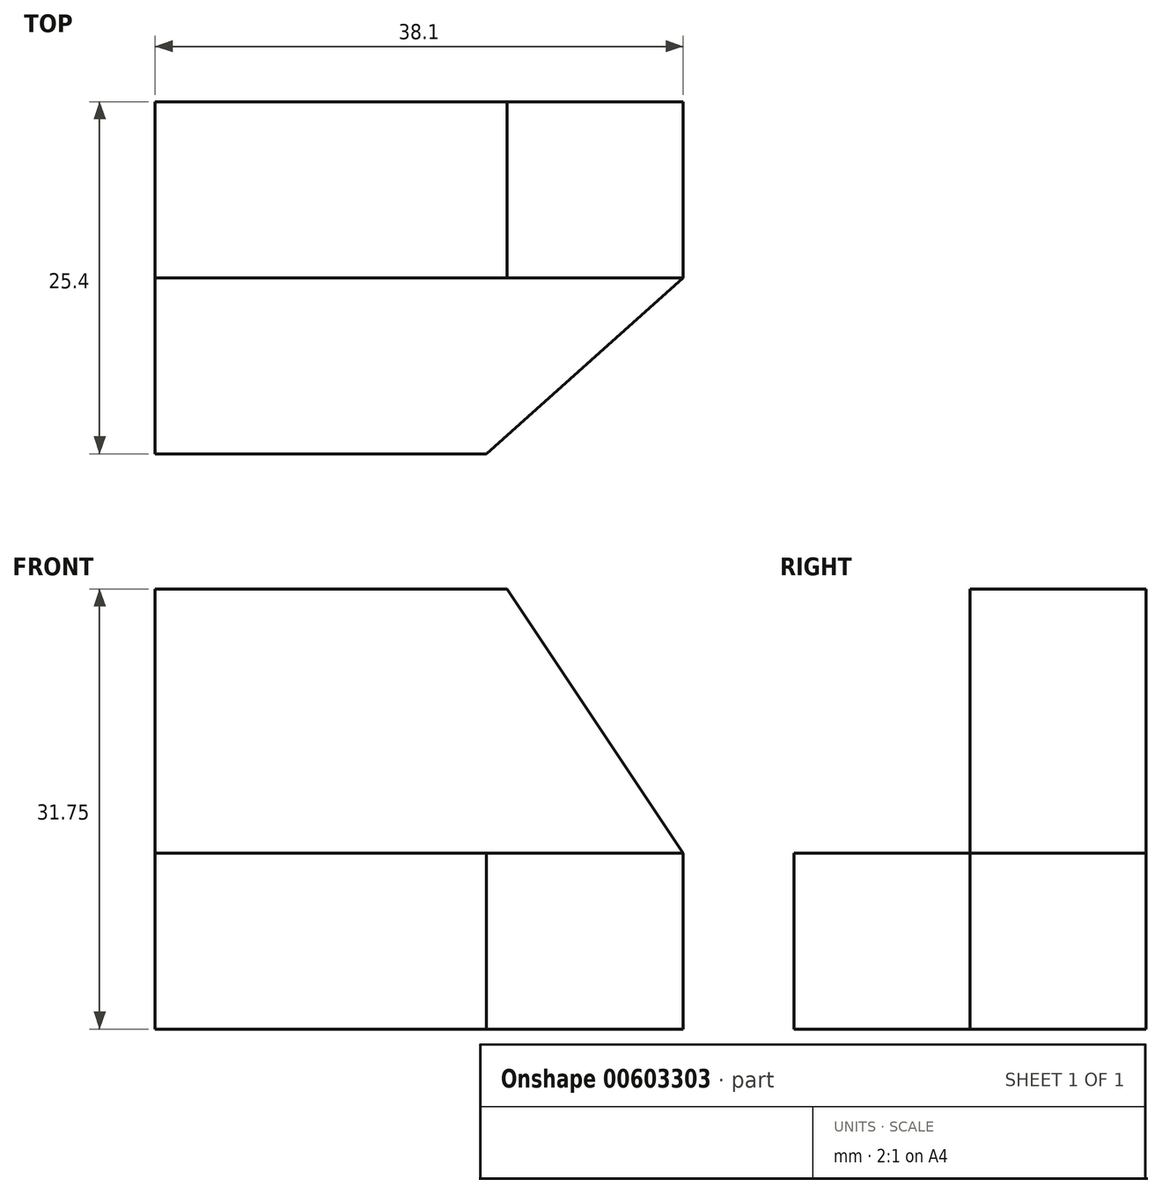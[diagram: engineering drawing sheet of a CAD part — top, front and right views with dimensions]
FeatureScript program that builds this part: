
annotation { "Feature Type Name" : "Feature", "Feature Type Description" : "" }
export const myFeature = defineFeature(function(context is Context, id is Id, definition is map)
    precondition{}
    {
        {
            var Q0;
            Q0=qCreatedBy(makeId("Front.planeOp"),FACE);
            var sketch = newSketch(context, id + "F0", { "sketchPlane" : qUnion([Q0])});
            skLineSegment(sketch, "E0", {"start": v(0, 0) * mm, "end": v(-19.05, 0) * mm});
            skLineSegment(sketch, "E1", {"start": v(-19.05, 0) * mm, "end": v(19.05, 0) * mm});
            skLineSegment(sketch, "E2", {"start": v(19.05, 0) * mm, "end": v(19.05, -31.75) * mm});
            skLineSegment(sketch, "E3", {"start": v(19.05, -31.75) * mm, "end": v(-19.05, -31.75) * mm});
            skLineSegment(sketch, "E4", {"start": v(-19.05, -31.75) * mm, "end": v(-19.05, 0) * mm});
            skSolve(sketch);
        }
        {
            var Q0;
            Q0 = qSketchRegion(id + "F0", true);
            extrude(context, id + "F1", {"entities" : qUnion([Q0]), "depth" : 25.4 * mm, "offsetDistance" : 25.4 * mm});
        }
        {
            var Q0;
            Q0=makeQuery(id+"F1.opExtrude","SWEPT_FACE",FACE,{"disambiguationData":[OSD([sQuery(id+"F0.wireOp",EDGE,"E1")])]});
            var sketch = newSketch(context, id + "F2", { "sketchPlane" : qUnion([Q0])});
            skLineSegment(sketch, "E5", {"start": v(19.05, -25.4) * mm, "end": v(19.05, -12.7) * mm});
            skLineSegment(sketch, "E6", {"start": v(19.05, -12.7) * mm, "end": v(-19.05, -12.7) * mm});
            skLineSegment(sketch, "E7", {"start": v(-19.05, -12.7) * mm, "end": v(-19.05, -25.4) * mm});
            skLineSegment(sketch, "E8", {"start": v(-19.05, -25.4) * mm, "end": v(19.05, -25.4) * mm});
            skSolve(sketch);
        }
        {
            var Q0;
            Q0 = qSketchRegion(id + "F2", true);
            extrude(context, id + "F3", {"entities" : qUnion([Q0]), "operationType" : NewBodyOperationType.REMOVE, "oppositeDirection" : true, "depth" : 19.05 * mm, "offsetDistance" : 25.4 * mm});
        }
        {
            var Q0;
            Q0=makeQuery(id+"F3.boolean.opBoolean","COPY",FACE,{"derivedFrom":makeQuery(id+"F3.opExtrude","CAP_FACE",FACE,{"disambiguationData":[OSD([sQuery(id+"F2.wireOp",EDGE,"E5"),sQuery(id+"F2.wireOp",EDGE,"E6"),sQuery(id+"F2.wireOp",EDGE,"E7"),sQuery(id+"F2.wireOp",EDGE,"E8")])],"isStart":false})});
            var sketch = newSketch(context, id + "F4", { "sketchPlane" : qUnion([Q0])});
            skLineSegment(sketch, "E9", {"start": v(19.05, -12.7) * mm, "end": v(4.85, -25.4) * mm});
            skLineSegment(sketch, "E10", {"start": v(4.85, -25.4) * mm, "end": v(19.05, -25.4) * mm});
            skLineSegment(sketch, "E11", {"start": v(19.05, -25.4) * mm, "end": v(19.05, -12.7) * mm});
            skSolve(sketch);
        }
        {
            var Q0;
            Q0 = qSketchRegion(id + "F4", true);
            extrude(context, id + "F5", {"entities" : qUnion([Q0]), "operationType" : NewBodyOperationType.REMOVE, "oppositeDirection" : true, "depth" : 25.4 * mm, "offsetDistance" : 25.4 * mm});
        }
        {
            var Q0;
            Q0=makeQuery(id+"F3.boolean.opBoolean","COPY",FACE,{"derivedFrom":makeQuery(id+"F3.opExtrude","SWEPT_FACE",FACE,{"disambiguationData":[OSD([sQuery(id+"F2.wireOp",EDGE,"E6")])]})});
            var sketch = newSketch(context, id + "F6", { "sketchPlane" : qUnion([Q0])});
            skLineSegment(sketch, "E12", {"start": v(19.05, 0) * mm, "end": v(6.35, 0) * mm});
            skLineSegment(sketch, "E13", {"start": v(6.35, 0) * mm, "end": v(19.05, -19.05) * mm});
            skLineSegment(sketch, "E14", {"start": v(19.05, -19.05) * mm, "end": v(19.05, 0) * mm});
            skSolve(sketch);
        }
        {
            var Q0;
            Q0 = qSketchRegion(id + "F6", true);
            extrude(context, id + "F7", {"entities" : qUnion([Q0]), "operationType" : NewBodyOperationType.REMOVE, "oppositeDirection" : true, "depth" : 25.4 * mm, "offsetDistance" : 25.4 * mm});
        }
    });
